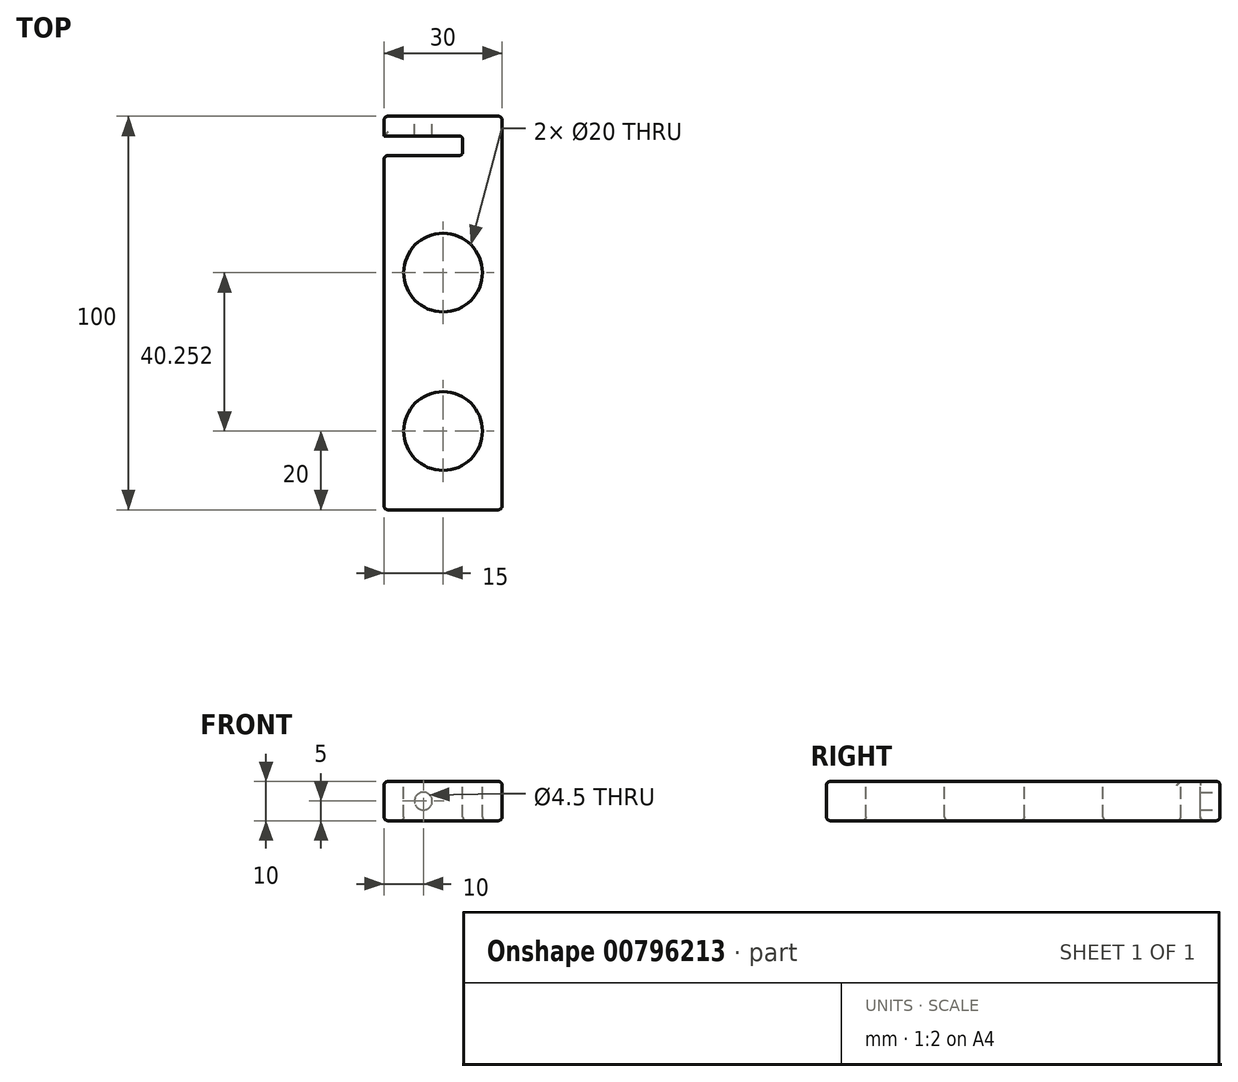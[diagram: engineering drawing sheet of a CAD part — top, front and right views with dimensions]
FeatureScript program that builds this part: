
annotation { "Feature Type Name" : "Feature", "Feature Type Description" : "" }
export const myFeature = defineFeature(function(context is Context, id is Id, definition is map)
    precondition{}
    {
        {
            var Q0;
            Q0=qCreatedBy(makeId("Top.planeOp"),FACE);
            var sketch = newSketch(context, id + "F0", { "sketchPlane" : qUnion([Q0])});
            skLineSegment(sketch, "E0.bottom", {"start": v(-15, 50) * mm, "end": v(15, 50) * mm});
            skLineSegment(sketch, "E0.top", {"start": v(-15, -50) * mm, "end": v(15, -50) * mm});
            skLineSegment(sketch, "E0.left", {"start": v(-15, 50) * mm, "end": v(-15, -50) * mm});
            skLineSegment(sketch, "E0.right", {"start": v(15, 50) * mm, "end": v(15, -50) * mm});
            skPoint(sketch, "E0.middle", {"position": v(0, 0) * mm});
            skSolve(sketch);
        }
        {
            var Q0;
            Q0 = qSketchRegion(id + "F0", true);
            extrude(context, id + "F1", {"entities" : qUnion([Q0]), "depth" : 10 * mm, "offsetDistance" : 25 * mm});
        }
        {
            var Q0;
            Q0=makeQuery(id+"F1.opExtrude","CAP_FACE",FACE,{"disambiguationData":[OSD([sQuery(id+"F0.wireOp",EDGE,"E0.bottom"),sQuery(id+"F0.wireOp",EDGE,"E0.top"),sQuery(id+"F0.wireOp",EDGE,"E0.left"),sQuery(id+"F0.wireOp",EDGE,"E0.right")])],"isStart":false});
            var sketch = newSketch(context, id + "F2", { "sketchPlane" : qUnion([Q0])});
            skLineSegment(sketch, "E1", {"start": v(-15, 45) * mm, "end": v(5, 45) * mm});
            skLineSegment(sketch, "E2", {"start": v(5, 45) * mm, "end": v(5, 40) * mm});
            skLineSegment(sketch, "E3", {"start": v(5, 40) * mm, "end": v(-15, 40) * mm});
            skLineSegment(sketch, "E4", {"start": v(-15, 40) * mm, "end": v(-15, 45) * mm});
            skSolve(sketch);
        }
        {
            var Q0;
            Q0=makeQuery(id+"F2.imprint","IMPRINT",FACE,{"disambiguationData":[TD([[makeQuery(id+"F2.imprint","IMPRINT",EDGE,{"derivedFrom":sQuery(id+"F2.wireOp",EDGE,"E1")}),-1.0]])]});
            extrude(context, id + "F3", {"entities" : qUnion([Q0]), "operationType" : NewBodyOperationType.REMOVE, "oppositeDirection" : true, "depth" : 25 * mm, "offsetDistance" : 25 * mm});
        }
        {
            var Q0;
            Q0=makeQuery(id+"F1.opExtrude","SWEPT_FACE",FACE,{"disambiguationData":[OSD([sQuery(id+"F0.wireOp",EDGE,"E0.bottom")])]});
            var sketch = newSketch(context, id + "F4", { "sketchPlane" : qUnion([Q0])});
            skLineSegment(sketch, "E5", {"start": v(15, 5) * mm, "end": v(5, 5) * mm});
            skCircle(sketch, "E6", {"center": v(5, 5) * mm, "radius": 2.25 * mm});
            skSolve(sketch);
        }
        {
            var Q0;
            Q0 = qSketchRegion(id + "F4", true);
            extrude(context, id + "F5", {"entities" : qUnion([Q0]), "operationType" : NewBodyOperationType.REMOVE, "oppositeDirection" : true, "depth" : 6 * mm, "offsetDistance" : 25 * mm});
        }
        {
            var Q0;
            Q0=makeQuery(id+"F3.boolean.opBoolean","COPY",EDGE,{"derivedFrom":makeQuery(id+"F3.opExtrude","SWEPT_EDGE",EDGE,{"disambiguationData":[OSD([sQuery(id+"F0.wireOp",EDGE,"E0.left"),sQuery(id+"F2.wireOp",EDGE,"E1"),sQuery(id+"F2.wireOp",EDGE,"E4")])]})});
            var Q1;
            Q1=makeQuery(id+"F1.opExtrude","SWEPT_EDGE",EDGE,{"disambiguationData":[OSD([sQuery(id+"F0.wireOp",EDGE,"E0.bottom"),sQuery(id+"F0.wireOp",EDGE,"E0.left")])]});
            fillet(context, id + "F6", {"entities" : qUnion([Q0, Q1]), "radius" : 1 * mm, "tangentPropagation" : true, "allowEdgeOverflow" : false});
        }
        {
            var Q0;
            Q0=makeQuery(id+"F3.boolean.opBoolean","COPY",EDGE,{"derivedFrom":makeQuery(id+"F3.opExtrude","SWEPT_EDGE",EDGE,{"disambiguationData":[OSD([sQuery(id+"F0.wireOp",EDGE,"E0.left"),sQuery(id+"F2.wireOp",EDGE,"E3"),sQuery(id+"F2.wireOp",EDGE,"E4")])]})});
            var Q1;
            Q1=makeQuery(id+"F3.boolean.opBoolean","COPY",EDGE,{"derivedFrom":makeQuery(id+"F3.opExtrude","SWEPT_EDGE",EDGE,{"disambiguationData":[OSD([sQuery(id+"F2.wireOp",EDGE,"E2"),sQuery(id+"F2.wireOp",EDGE,"E3")])]})});
            var Q2;
            Q2=makeQuery(id+"F3.boolean.opBoolean","COPY",EDGE,{"derivedFrom":makeQuery(id+"F3.opExtrude","SWEPT_EDGE",EDGE,{"disambiguationData":[OSD([sQuery(id+"F2.wireOp",EDGE,"E1"),sQuery(id+"F2.wireOp",EDGE,"E2")])]})});
            var Q3;
            Q3=makeQuery(id+"F1.opExtrude","SWEPT_EDGE",EDGE,{"disambiguationData":[OSD([sQuery(id+"F0.wireOp",EDGE,"E0.bottom"),sQuery(id+"F0.wireOp",EDGE,"E0.right")])]});
            var Q4;
            Q4=makeQuery(id+"F1.opExtrude","SWEPT_EDGE",EDGE,{"disambiguationData":[OSD([sQuery(id+"F0.wireOp",EDGE,"E0.top"),sQuery(id+"F0.wireOp",EDGE,"E0.right")])]});
            var Q5;
            Q5=makeQuery(id+"F1.opExtrude","SWEPT_EDGE",EDGE,{"disambiguationData":[OSD([sQuery(id+"F0.wireOp",EDGE,"E0.top"),sQuery(id+"F0.wireOp",EDGE,"E0.left")])]});
            var Q6;
            {var subQ0=sQuery(id+"F0.wireOp",EDGE,"E0.left");var subQ1=sQuery(id+"F0.wireOp",EDGE,"E0.top");Q6=makeQuery(id+"F3.boolean.opBoolean","SPLIT",EDGE,{"disambiguationData":[TD([makeQuery(id+"F1.opExtrude","SWEPT_FACE",FACE,{"disambiguationData":[OSD([subQ1])]})])],"derivedFrom":makeQuery(id+"F1.opExtrude","CAP_EDGE",EDGE,{"disambiguationData":[OSD([subQ0])],"isStart":false})});}
            var Q7;
            Q7=makeQuery(id+"F1.opExtrude","CAP_EDGE",EDGE,{"disambiguationData":[OSD([sQuery(id+"F0.wireOp",EDGE,"E0.right")])],"isStart":false});
            var Q8;
            Q8=makeQuery(id+"F1.opExtrude","SWEPT_FACE",FACE,{"disambiguationData":[OSD([sQuery(id+"F0.wireOp",EDGE,"E0.right")])]});
            var Q9;
            Q9=makeQuery(id+"F1.opExtrude","CAP_EDGE",EDGE,{"disambiguationData":[OSD([sQuery(id+"F0.wireOp",EDGE,"E0.top")])],"isStart":true});
            var Q10;
            Q10=makeQuery(id+"F1.opExtrude","CAP_FACE",FACE,{"disambiguationData":[OSD([sQuery(id+"F0.wireOp",EDGE,"E0.bottom"),sQuery(id+"F0.wireOp",EDGE,"E0.top"),sQuery(id+"F0.wireOp",EDGE,"E0.left"),sQuery(id+"F0.wireOp",EDGE,"E0.right")])],"isStart":true});
            var Q11;
            Q11=makeQuery(id+"F1.opExtrude","CAP_EDGE",EDGE,{"disambiguationData":[OSD([sQuery(id+"F0.wireOp",EDGE,"E0.bottom")])],"isStart":false});
            fillet(context, id + "F7", {"entities" : qUnion([Q0, Q1, Q2, Q3, Q4, Q5, Q6, Q7, Q8, Q9, Q10, Q11]), "radius" : 1 * mm, "tangentPropagation" : true, "allowEdgeOverflow" : false});
        }
        {
            var Q0;
            Q0=makeQuery(id+"F1.opExtrude","CAP_EDGE",EDGE,{"disambiguationData":[OSD([sQuery(id+"F0.wireOp",EDGE,"E0.top")])],"isStart":false});
            fillet(context, id + "F8", {"entities" : qUnion([Q0]), "radius" : 1 * mm, "tangentPropagation" : true, "allowEdgeOverflow" : false});
        }
        {
            var Q0;
            Q0=makeQuery(id+"F1.opExtrude","CAP_FACE",FACE,{"disambiguationData":[OSD([sQuery(id+"F0.wireOp",EDGE,"E0.bottom"),sQuery(id+"F0.wireOp",EDGE,"E0.top"),sQuery(id+"F0.wireOp",EDGE,"E0.left"),sQuery(id+"F0.wireOp",EDGE,"E0.right")])],"isStart":false});
            var sketch = newSketch(context, id + "F9", { "sketchPlane" : qUnion([Q0])});
            skLineSegment(sketch, "E7", {"start": v(0, -49) * mm, "end": v(0, -30) * mm});
            skCircle(sketch, "E8", {"center": v(0, -30) * mm, "radius": 10 * mm});
            skLineSegment(sketch, "E9", {"start": v(0, -30) * mm, "end": v(0, 10.25) * mm});
            skCircle(sketch, "E10", {"center": v(0, 10.25) * mm, "radius": 10 * mm});
            skSolve(sketch);
        }
        {
            var Q0;
            Q0 = qSketchRegion(id + "F9", true);
            extrude(context, id + "F10", {"entities" : qUnion([Q0]), "operationType" : NewBodyOperationType.REMOVE, "oppositeDirection" : true, "depth" : 25 * mm, "offsetDistance" : 25 * mm});
        }
        {
            var Q0;
            Q0=makeQuery(id+"F10.boolean.opBoolean","INTERSECT",EDGE,{"derivedFrom":[makeQuery(id+"F1.opExtrude","CAP_FACE",FACE,{"disambiguationData":[OSD([sQuery(id+"F0.wireOp",EDGE,"E0.bottom"),sQuery(id+"F0.wireOp",EDGE,"E0.top"),sQuery(id+"F0.wireOp",EDGE,"E0.left"),sQuery(id+"F0.wireOp",EDGE,"E0.right")])],"isStart":true}),makeQuery(id+"F10.opExtrude","SWEPT_FACE",FACE,{"disambiguationData":[OSD([sQuery(id+"F9.wireOp",EDGE,"E8")])]})]});
            fillet(context, id + "F11", {"entities" : qUnion([Q0]), "radius" : 1 * mm, "tangentPropagation" : true, "allowEdgeOverflow" : false});
        }
        {
            var Q0;
            Q0=makeQuery(id+"F10.boolean.opBoolean","COPY",EDGE,{"derivedFrom":makeQuery(id+"F10.opExtrude","CAP_EDGE",EDGE,{"disambiguationData":[OSD([sQuery(id+"F9.wireOp",EDGE,"E8")])],"isStart":true})});
            var Q1;
            Q1=makeQuery(id+"F10.boolean.opBoolean","COPY",EDGE,{"derivedFrom":makeQuery(id+"F10.opExtrude","CAP_EDGE",EDGE,{"disambiguationData":[OSD([sQuery(id+"F9.wireOp",EDGE,"E10")])],"isStart":true})});
            var Q2;
            Q2=makeQuery(id+"F10.boolean.opBoolean","INTERSECT",EDGE,{"derivedFrom":[makeQuery(id+"F1.opExtrude","CAP_FACE",FACE,{"disambiguationData":[OSD([sQuery(id+"F0.wireOp",EDGE,"E0.bottom"),sQuery(id+"F0.wireOp",EDGE,"E0.top"),sQuery(id+"F0.wireOp",EDGE,"E0.left"),sQuery(id+"F0.wireOp",EDGE,"E0.right")])],"isStart":true}),makeQuery(id+"F10.opExtrude","SWEPT_FACE",FACE,{"disambiguationData":[OSD([sQuery(id+"F9.wireOp",EDGE,"E10")])]})]});
            fillet(context, id + "F12", {"entities" : qUnion([Q0, Q1, Q2]), "radius" : 1 * mm, "tangentPropagation" : true, "allowEdgeOverflow" : false});
        }
    });
